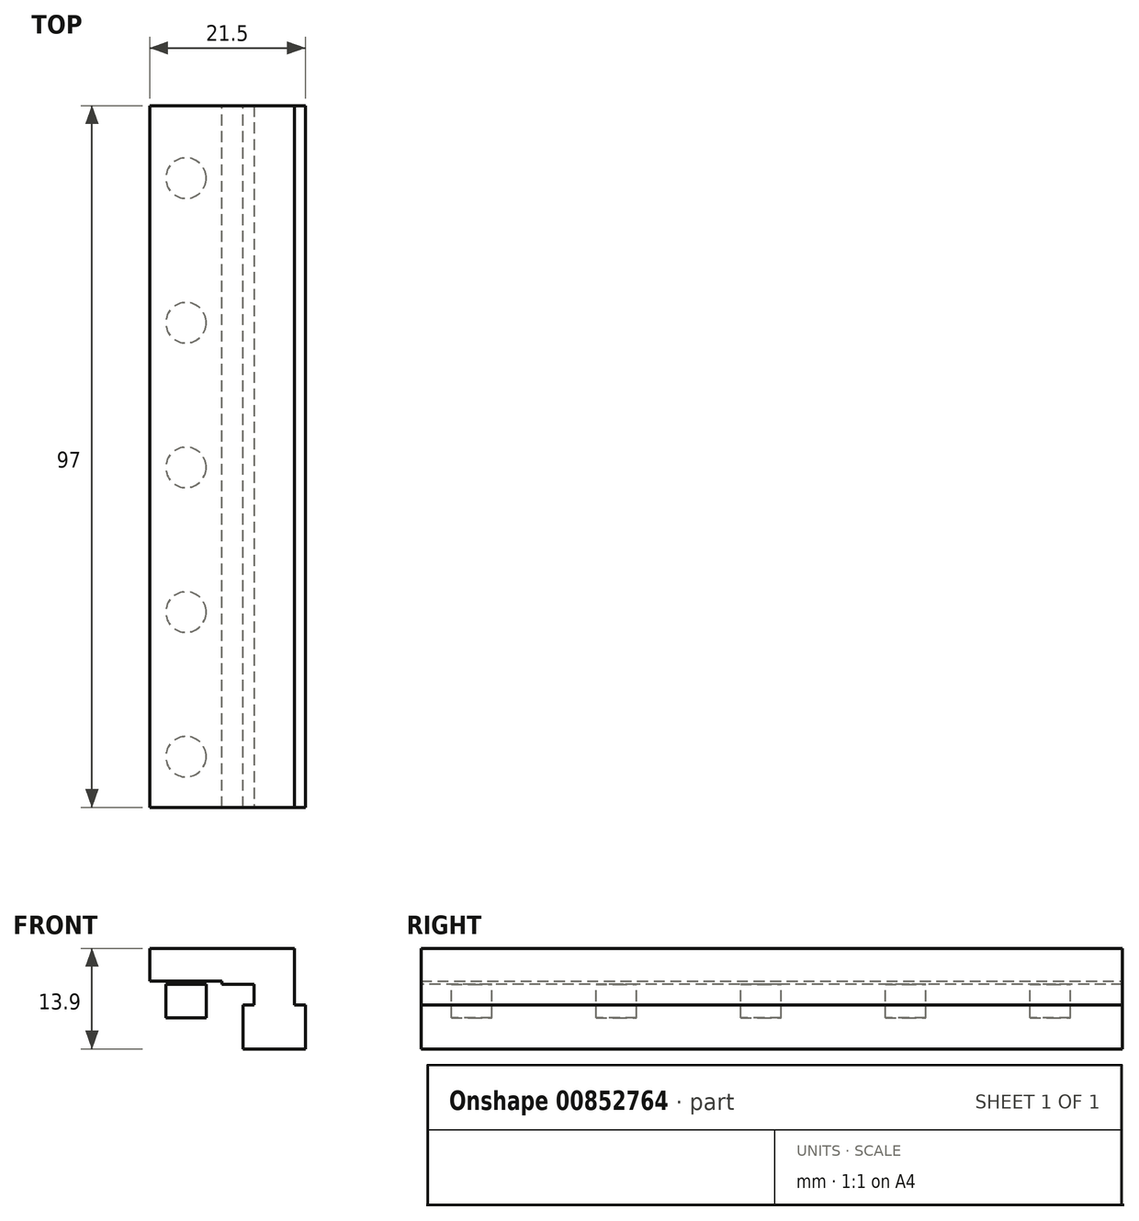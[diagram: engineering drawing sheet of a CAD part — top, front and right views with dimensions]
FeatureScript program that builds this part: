
annotation { "Feature Type Name" : "Feature", "Feature Type Description" : "" }
export const myFeature = defineFeature(function(context is Context, id is Id, definition is map)
    precondition{}
    {
        {
            var Q0;
            Q0=qCreatedBy(makeId("Top.planeOp"),FACE);
            var sketch = newSketch(context, id + "F0", { "sketchPlane" : qUnion([Q0])});
            skLineSegment(sketch, "E0.bottom", {"start": v(4.3, -48.5) * mm, "end": v(-4.3, -48.5) * mm});
            skLineSegment(sketch, "E0.top", {"start": v(4.3, 48.5) * mm, "end": v(-4.3, 48.5) * mm});
            skLineSegment(sketch, "E0.left", {"start": v(4.3, -48.5) * mm, "end": v(4.3, 48.5) * mm});
            skLineSegment(sketch, "E0.right", {"start": v(-4.3, -48.5) * mm, "end": v(-4.3, 48.5) * mm});
            skPoint(sketch, "E0.middle", {"position": v(0, 0) * mm});
            skSolve(sketch);
        }
        {
            var Q0;
            Q0 = qSketchRegion(id + "F0", true);
            var Q1;
            Q1=makeQuery(id+"F0.imprint","IMPRINT",FACE,{"disambiguationData":[TD([[makeQuery(id+"F0.imprint","IMPRINT",EDGE,{"derivedFrom":sQuery(id+"F0.wireOp",EDGE,"E0.bottom")}),-1.0]])]});
            extrude(context, id + "F1", {"entities" : qUnion([Q0, Q1]), "depth" : 6.1 * mm, "offsetDistance" : 25 * mm});
        }
        {
            var Q0;
            Q0=makeQuery(id+"F1.opExtrude","CAP_FACE",FACE,{"disambiguationData":[OSD([sQuery(id+"F0.wireOp",EDGE,"E0.bottom"),sQuery(id+"F0.wireOp",EDGE,"E0.top"),sQuery(id+"F0.wireOp",EDGE,"E0.left"),sQuery(id+"F0.wireOp",EDGE,"E0.right")])],"isStart":false});
            var sketch = newSketch(context, id + "F2", { "sketchPlane" : qUnion([Q0])});
            skPoint(sketch, "E1.0", {"position": v(0, 0) * mm});
            skLineSegment(sketch, "E2.bottom", {"start": v(-2.8, 48.5) * mm, "end": v(2.8, 48.5) * mm});
            skLineSegment(sketch, "E2.top", {"start": v(-2.8, -48.5) * mm, "end": v(2.8, -48.5) * mm});
            skLineSegment(sketch, "E2.left", {"start": v(-2.8, 48.5) * mm, "end": v(-2.8, -48.5) * mm});
            skLineSegment(sketch, "E2.right", {"start": v(2.8, 48.5) * mm, "end": v(2.8, -48.5) * mm});
            skSolve(sketch);
        }
        {
            var Q0;
            Q0=makeQuery(id+"F2.imprint","IMPRINT",FACE,{"disambiguationData":[TD([[makeQuery(id+"F2.imprint","IMPRINT",EDGE,{"derivedFrom":sQuery(id+"F2.wireOp",EDGE,"E2.bottom")}),1.0]])]});
            extrude(context, id + "F3", {"entities" : qUnion([Q0]), "operationType" : NewBodyOperationType.ADD, "depth" : 2.8 * mm, "offsetDistance" : 25 * mm});
        }
        {
            var Q0;
            Q0=makeQuery(id+"F3.opExtrude","CAP_FACE",FACE,{"disambiguationData":[OSD([sQuery(id+"F2.wireOp",EDGE,"E2.bottom"),sQuery(id+"F2.wireOp",EDGE,"E2.top"),sQuery(id+"F2.wireOp",EDGE,"E2.left"),sQuery(id+"F2.wireOp",EDGE,"E2.right")])],"isStart":false});
            var sketch = newSketch(context, id + "F4", { "sketchPlane" : qUnion([Q0])});
            skLineSegment(sketch, "E3.0", {"start": v(-4.3, -48.5) * mm, "end": v(-4.3, 48.5) * mm});
            skPoint(sketch, "E4.0", {"position": v(2.8, -48.5) * mm});
            skPoint(sketch, "E4.1", {"position": v(2.8, 48.5) * mm});
            skLineSegment(sketch, "E5.0", {"start": v(-7.2, -48.5) * mm, "end": v(-7.2, 48.5) * mm});
            skLineSegment(sketch, "E6.0", {"start": v(-17.2, -48.5) * mm, "end": v(-17.2, 48.5) * mm});
            skLineSegment(sketch, "E7", {"start": v(-17.2, -48.5) * mm, "end": v(2.8, -48.5) * mm});
            skLineSegment(sketch, "E8", {"start": v(-17.2, 48.5) * mm, "end": v(2.8, 48.5) * mm});
            skSolve(sketch);
        }
        {
            var Q0;
            {var subQ0=sQuery(id+"F4.wireOp",EDGE,"E5.0");Q0=makeQuery(id+"F4.imprint","IMPRINT",FACE,{"disambiguationData":[TD([[makeQuery(id+"F4.imprint","IMPRINT",EDGE,{"derivedFrom":subQ0}),1.0]])]});}
            var Q1;
            {var subQ2=makeQuery(id+"F3.opExtrude","CAP_EDGE",EDGE,{"disambiguationData":[OSD([sQuery(id+"F2.wireOp",EDGE,"E2.left")])],"isStart":false});Q1=makeQuery(id+"F4.imprint","IMPRINT",FACE,{"disambiguationData":[TD([[makeQuery(id+"F4.imprint","IMPRINT",EDGE,{"derivedFrom":subQ2}),1.0]])]});}
            var Q2;
            {var subQ0=sQuery(id+"F4.wireOp",EDGE,"E3.0");Q2=makeQuery(id+"F4.imprint","IMPRINT",FACE,{"disambiguationData":[TD([[makeQuery(id+"F4.imprint","IMPRINT",EDGE,{"derivedFrom":subQ0}),-1.0]])]});}
            var Q3;
            {var subQ0=sQuery(id+"F4.wireOp",EDGE,"E3.0");Q3=makeQuery(id+"F4.imprint","IMPRINT",FACE,{"disambiguationData":[TD([[makeQuery(id+"F4.imprint","IMPRINT",EDGE,{"derivedFrom":subQ0}),1.0]])]});}
            extrude(context, id + "F5", {"entities" : qUnion([Q0, Q1, Q2, Q3]), "operationType" : NewBodyOperationType.ADD, "depth" : 5 * mm, "offsetDistance" : 25 * mm});
        }
        {
            var Q0;
            {var subQ0=sQuery(id+"F4.wireOp",EDGE,"E5.0");Q0=makeQuery(id+"F4.imprint","IMPRINT",FACE,{"disambiguationData":[TD([[makeQuery(id+"F4.imprint","IMPRINT",EDGE,{"derivedFrom":subQ0}),1.0]])]});}
            extrude(context, id + "F6", {"entities" : qUnion([Q0]), "operationType" : NewBodyOperationType.REMOVE, "oppositeDirection" : true, "depth" : -0.5 * mm, "offsetDistance" : 25 * mm});
        }
        {
            var Q0;
            {var subQ0=sQuery(id+"F4.wireOp",EDGE,"E5.0");Q0=makeQuery(id+"F4.imprint","IMPRINT",FACE,{"disambiguationData":[TD([[makeQuery(id+"F4.imprint","IMPRINT",EDGE,{"derivedFrom":subQ0}),1.0]])]});}
            var sketch = newSketch(context, id + "F7", { "sketchPlane" : qUnion([Q0])});
            skLineSegment(sketch, "E9.0", {"start": v(-17.2, -48.5) * mm, "end": v(-17.2, 48.5) * mm, "construction": true});
            skLineSegment(sketch, "E10.0", {"start": v(-12.2, -48.5) * mm, "end": v(-12.2, 48.5) * mm, "construction": true});
            skLineSegment(sketch, "E11", {"start": v(-12.2, 48.5) * mm, "end": v(-12.2, 38.5) * mm, "construction": true});
            skCircle(sketch, "E12", {"center": v(-12.2, 38.5) * mm, "radius": 2.8 * mm});
            skLineSegment(sketch, "E13.1", {"start": v(-17.2, 48.5) * mm, "end": v(2.8, 48.5) * mm});
            skLineSegment(sketch, "E14", {"start": v(-12.2, 38.5) * mm, "end": v(-12.2, 18.5) * mm, "construction": true});
            skCircle(sketch, "E15", {"center": v(-12.2, 18.5) * mm, "radius": 2.8 * mm});
            skLineSegment(sketch, "E16", {"start": v(-12.2, -1.5) * mm, "end": v(-12.2, -21.5) * mm, "construction": true});
            skCircle(sketch, "E17", {"center": v(-12.2, -21.5) * mm, "radius": 2.8 * mm});
            skLineSegment(sketch, "E18", {"start": v(-12.2, 18.5) * mm, "end": v(-12.2, -1.5) * mm, "construction": true});
            skCircle(sketch, "E19", {"center": v(-12.2, -1.5) * mm, "radius": 2.8 * mm});
            skLineSegment(sketch, "E20", {"start": v(-12.2, -21.5) * mm, "end": v(-12.2, -41.5) * mm, "construction": true});
            skCircle(sketch, "E21", {"center": v(-12.2, -41.5) * mm, "radius": 2.8 * mm});
            skSolve(sketch);
        }
        {
            var Q0;
            Q0=makeQuery(id+"F7.imprint","IMPRINT",FACE,{"disambiguationData":[TD([[makeQuery(id+"F7.imprint","IMPRINT",EDGE,{"derivedFrom":sQuery(id+"F7.wireOp",EDGE,"E15")}),1.0]])]});
            var Q1;
            Q1=makeQuery(id+"F7.imprint","IMPRINT",FACE,{"disambiguationData":[TD([[makeQuery(id+"F7.imprint","IMPRINT",EDGE,{"derivedFrom":sQuery(id+"F7.wireOp",EDGE,"E19")}),1.0]])]});
            var Q2;
            Q2=makeQuery(id+"F7.imprint","IMPRINT",FACE,{"disambiguationData":[TD([[makeQuery(id+"F7.imprint","IMPRINT",EDGE,{"derivedFrom":sQuery(id+"F7.wireOp",EDGE,"E17")}),1.0]])]});
            var Q3;
            Q3=makeQuery(id+"F7.imprint","IMPRINT",FACE,{"disambiguationData":[TD([[makeQuery(id+"F7.imprint","IMPRINT",EDGE,{"derivedFrom":sQuery(id+"F7.wireOp",EDGE,"E21")}),1.0]])]});
            var Q4;
            Q4=makeQuery(id+"F7.imprint","IMPRINT",FACE,{"disambiguationData":[TD([[makeQuery(id+"F7.imprint","IMPRINT",EDGE,{"derivedFrom":sQuery(id+"F7.wireOp",EDGE,"E12")}),1.0]])]});
            extrude(context, id + "F8", {"entities" : qUnion([Q0, Q1, Q2, Q3, Q4]), "depth" : -4.6 * mm, "offsetDistance" : 25 * mm});
        }
    });
